# Revit family: TAG1
name_source: partatom
category: Furniture
units: mm (PartAtom-declared; Revit-internal decimal feet)

## family parameters
Always vertical = Yes
Cut with Voids When Loaded = No
OmniClass Number = 23.40.20.00
OmniClass Title = General Furniture and Specialties
Render Appearance Source = Family Geometry
Room Calculation Point = No
Shared = No
Work Plane-Based = No

## types (1)
- CW010
    Default Elevation = 0 mm  [stored 0 ft]
    Description = 1 x CaseWorks Backsplash Laminate 04Hx54W, 1 x CaseWorks Backsplash Laminate 04Hx91W, 9 x CaseWorks L-Bracket (Single) 5.5Hx1Wx1D, 2 x CaseWorks Countertop Support (Single) 21Hx1.75Wx24D, 1 x CaseWorks Countertop Laminate 24Dx54W, 1 x CaseWorks Countertop Laminate 24Dx91W, 2 x CaseWorks Full Height End Panel 34_5Hx24D (Cut to size on-site), 4 x CaseWorks Base Cabinet Side Filler 34_5HxWx6D (Cut to size on-site), 1 x CaseWorks Toe Kick 04Hx15W (Cut to size on-site), 1 x CaseWorks Toe Kick 04Hx90W (Cut to size on-site), 1 x CaseWorks Side Toe Kick 04Hx20.22W (Cut to size on-site), 1 x CaseWorks Base Cabinet Double Doors 35Hx36Wx24D, 1 x CaseWorks Base Cabinet Four Drawers 35Hx30Wx24D, 1 x CaseWorks Base Cabinet Trash Pullout 35Hx24Wx24D, 1 x CaseWorks Wardrobe Cabinet Single Door Right 84Hx15Wx24D, 3 x Soft Close Mechanism for Hinged Doors
    Exported From CET Designer = Yes
    Manufacturer = AIS
    Model = M-ABL0454
    Show CW010 = Yes
    VisibilityIndex = 0

note: [stored X ft] marks values corroborated as IEEE doubles in the binary element streams (Revit-internal decimal feet)

## geometry (parser evidence)
native form markers: Sweep x3
no freeform markers — native parametric forms only
